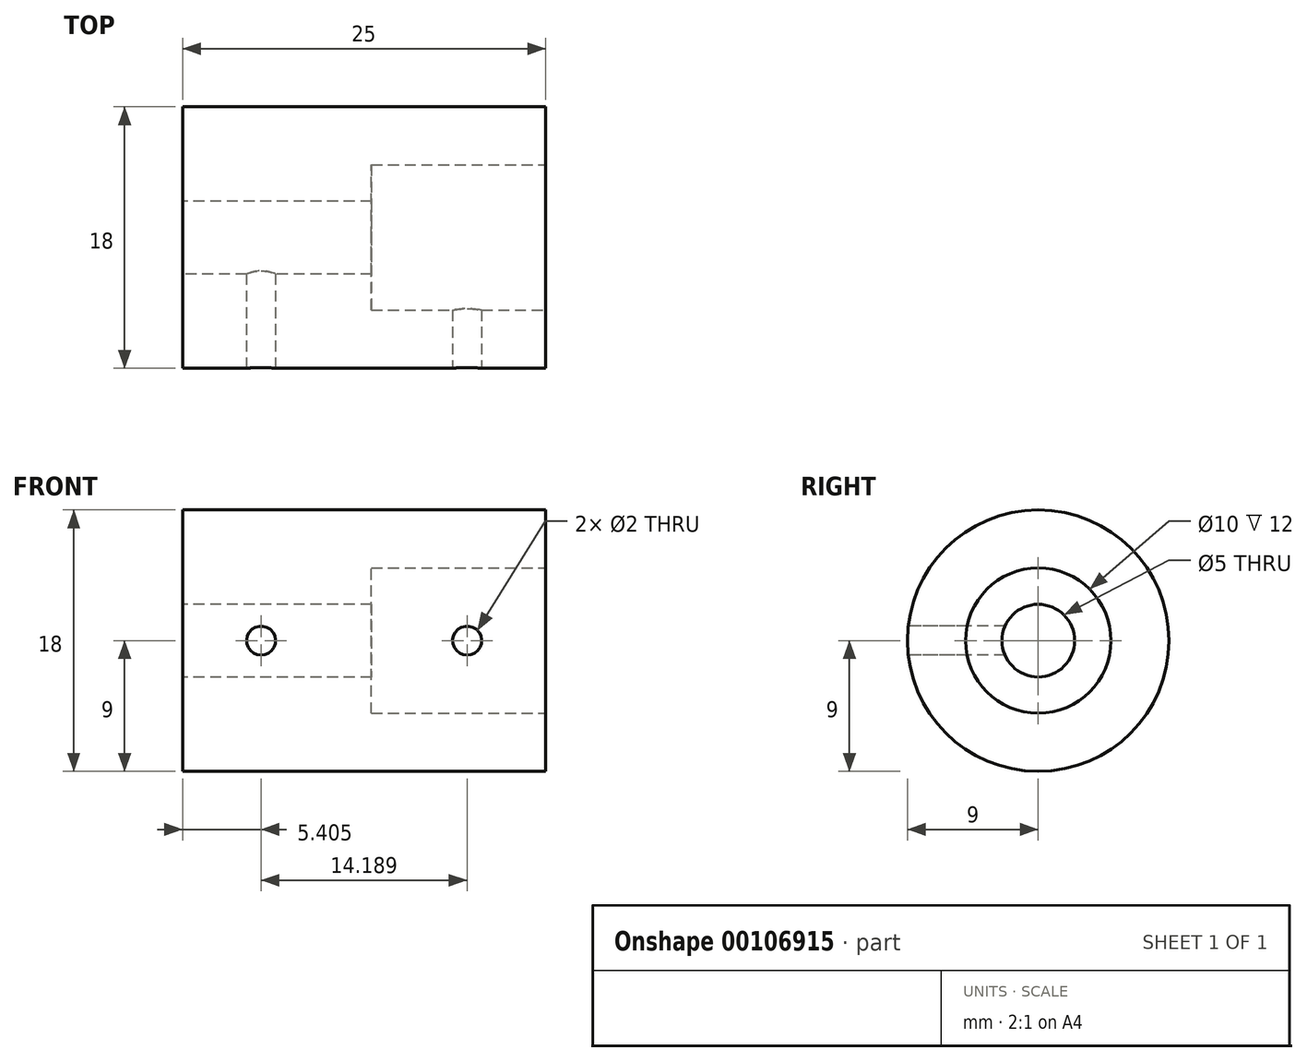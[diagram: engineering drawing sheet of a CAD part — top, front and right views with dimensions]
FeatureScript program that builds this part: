
annotation { "Feature Type Name" : "Feature", "Feature Type Description" : "" }
export const myFeature = defineFeature(function(context is Context, id is Id, definition is map)
    precondition{}
    {
        {
            var Q0;
            Q0=qCreatedBy(makeId("Right.planeOp"),FACE);
            var sketch = newSketch(context, id + "F0", { "sketchPlane" : qUnion([Q0])});
            skCircle(sketch, "E0", {"center": v(0, 0) * mm, "radius": 9 * mm});
            skSolve(sketch);
        }
        {
            var Q0;
            Q0 = qSketchRegion(id + "F0", true);
            extrude(context, id + "F1", {"entities" : qUnion([Q0]), "endBound" : BoundingType.SYMMETRIC, "depth" : 25 * mm});
        }
        {
            var Q0;
            Q0=makeQuery(id+"F1.opExtrude","CAP_FACE",FACE,{"disambiguationData":[OSD([sQuery(id+"F0.wireOp",EDGE,"E0")])],"isStart":false});
            var sketch = newSketch(context, id + "F2", { "sketchPlane" : qUnion([Q0])});
            skCircle(sketch, "E1", {"center": v(0, 0) * mm, "radius": 5 * mm});
            skSolve(sketch);
        }
        {
            var Q0;
            Q0 = qSketchRegion(id + "F2", true);
            extrude(context, id + "F3", {"entities" : qUnion([Q0]), "operationType" : NewBodyOperationType.REMOVE, "oppositeDirection" : true, "depth" : 12 * mm});
        }
        {
            var Q0;
            Q0=makeQuery(id+"F1.opExtrude","CAP_FACE",FACE,{"disambiguationData":[OSD([sQuery(id+"F0.wireOp",EDGE,"E0")])],"isStart":true});
            var sketch = newSketch(context, id + "F4", { "sketchPlane" : qUnion([Q0])});
            skCircle(sketch, "E2", {"center": v(0, 0) * mm, "radius": 2.5 * mm});
            skSolve(sketch);
        }
        {
            var Q0;
            Q0 = qSketchRegion(id + "F4", true);
            extrude(context, id + "F5", {"entities" : qUnion([Q0]), "operationType" : NewBodyOperationType.REMOVE, "oppositeDirection" : true, "depth" : 13 * mm});
        }
        {
            var Q0;
            Q0=qCreatedBy(makeId("Front.planeOp"),FACE);
            cPlane(context, id + "F6", {"entities" : qUnion([Q0]), "cplaneType" : CPlaneType.OFFSET, "offset" : 9 * mm, "width" : 150 * mm, "height" : 150 * mm});
        }
        {
            var Q0;
            Q0=qCreatedBy(id+"F6.planeOp",FACE);
            var sketch = newSketch(context, id + "F7", { "sketchPlane" : qUnion([Q0])});
            skCircle(sketch, "E3", {"center": v(7.1, 0) * mm, "radius": 1 * mm});
            skCircle(sketch, "E4.MirrorC", {"center": v(-7.1, 0) * mm, "radius": 1 * mm});
            skSolve(sketch);
        }
        {
            var Q0;
            Q0 = qSketchRegion(id + "F7", true);
            extrude(context, id + "F8", {"entities" : qUnion([Q0]), "operationType" : NewBodyOperationType.REMOVE, "oppositeDirection" : true, "depth" : 9 * mm});
        }
    });
